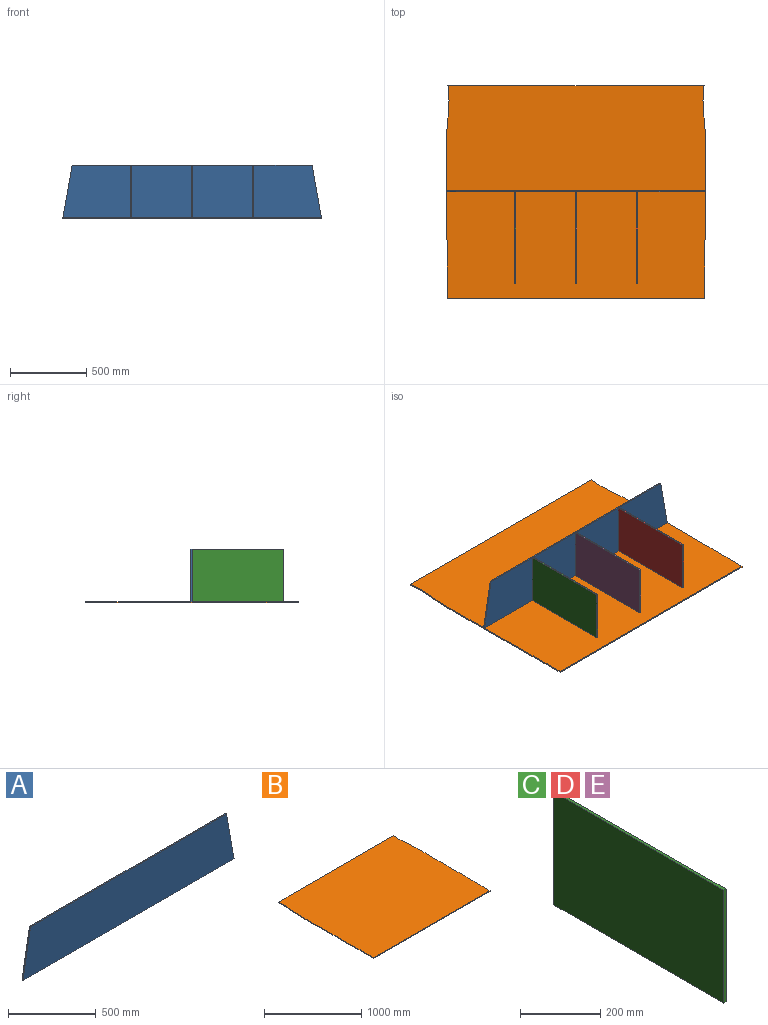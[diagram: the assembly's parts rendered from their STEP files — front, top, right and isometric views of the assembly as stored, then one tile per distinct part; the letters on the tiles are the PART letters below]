
ASSEMBLY  parts=5 mates=4
PART A: 6 faces, bbox 1700x8x344.7 mm
  f0: plane 1578.45x8mm, normal (0,0,1), area 12627.6mm2, adj f1,f3,f4,f5
  f1: plane 344.68x60.78mm, normal (-0.98,0,0.17), area 2800mm2, adj f0,f2,f4,f5
  f2: plane 1700x8mm, normal (0,0,-1), area 13600mm2, adj f1,f3,f4,f5
  f3: plane 344.68x60.78mm, normal (0.98,0,0.17), area 2800mm2, adj f0,f2,f4,f5
  f4: plane 1700x344.68mm, normal (0,-1,0), area 565011.9mm2, adj f0,f1,f2,f3
  f5: plane 1700x344.68mm, normal (0,1,0), area 565011.9mm2, adj f0,f1,f2,f3
PART B: 26 faces, bbox 1702x1400x8 mm
  f0: plane 1692x8mm, normal (0,-1,0), area 13536mm2, adj f1,f23,f24,f25
  f1: plane 100x8mm, normal (1,-0.01,0), area 800mm2, adj f0,f2,f24,f25
  f2: plane 100x8mm, normal (1,0,0), area 800mm2, adj f1,f3,f24,f25
  f3: plane 100x8mm, normal (1,-0.01,0), area 800mm2, adj f2,f4,f24,f25
  f4: plane 200x8mm, normal (1,0,0), area 1600mm2, adj f3,f5,f24,f25
  f5: plane 200x8mm, normal (1,0,0), area 1600mm2, adj f4,f6,f24,f25
  f6: plane 200x8mm, normal (1,-0.01,0), area 1600.1mm2, adj f5,f7,f24,f25
  f7: plane 100x8mm, normal (1,0,0), area 800mm2, adj f6,f8,f24,f25
  f8: plane 100x8mm, normal (1,0.01,0), area 800mm2, adj f7,f9,f24,f25
  f9: plane 100x9mm, normal (1,0.09,0), area 803.2mm2, adj f8,f10,f24,f25
  f10: plane 100x8mm, normal (1,0.06,0), area 801.4mm2, adj f9,f11,f24,f25
  f11: plane 100x8mm, normal (1,-0.07,0), area 802mm2, adj f10,f12,f24,f25
  f12: plane 1684x8mm, normal (0,1,0), area 13472mm2, adj f11,f13,f24,f25
  f13: plane 100x8mm, normal (-1,-0.07,0), area 802mm2, adj f12,f14,f24,f25
  f14: plane 100x8mm, normal (-1,0.06,0), area 801.4mm2, adj f13,f15,f24,f25
  f15: plane 100x9mm, normal (-1,0.09,0), area 803.2mm2, adj f14,f16,f24,f25
  f16: plane 100x8mm, normal (-1,0.01,0), area 800mm2, adj f15,f17,f24,f25
  f17: plane 100x8mm, normal (-1,0,0), area 800mm2, adj f16,f18,f24,f25
  f18: plane 200x8mm, normal (-1,-0.01,0), area 1600.1mm2, adj f17,f19,f24,f25
  f19: plane 200x8mm, normal (-1,0,0), area 1600mm2, adj f18,f20,f24,f25
  f20: plane 200x8mm, normal (-1,0,0), area 1600mm2, adj f19,f21,f24,f25
  f21: plane 100x8mm, normal (-1,-0.01,0), area 800mm2, adj f20,f22,f24,f25
  f22: plane 100x8mm, normal (-1,0,0), area 800mm2, adj f21,f23,f24,f25
  f23: plane 100x8mm, normal (-1,-0.01,0), area 800mm2, adj f0,f22,f24,f25
  f24: plane 1702x1400mm, normal (0,0,-1), area 2371900mm2, adj f0,f1,f2,f3,f4,f5,f6,f7
  f25: plane 1702x1400mm, normal (0,0,1), area 2371900mm2, adj f0,f1,f2,f3,f4,f5,f6,f7
PART C: 6 faces, bbox 8x600x344.7 mm
  f0: plane 600x8mm, normal (0,0,1), area 4800mm2, adj f1,f3,f4,f5
  f1: plane 344.68x8mm, normal (0,-1,0), area 2757.5mm2, adj f0,f2,f4,f5
  f2: plane 600x8mm, normal (0,0,-1), area 4800mm2, adj f1,f3,f4,f5
  f3: plane 344.68x8mm, normal (0,1,0), area 2757.5mm2, adj f0,f2,f4,f5
  f4: plane 600x344.68mm, normal (1,0,0), area 206809.6mm2, adj f0,f1,f2,f3
  f5: plane 600x344.68mm, normal (-1,0,0), area 206809.6mm2, adj f0,f1,f2,f3
PART D: same geometry as C
PART E: same geometry as C
PLACE A t=(3.79,605.93,181)mm
PLACE B t=(2.79,-2.07,181)mm
PLACE C t=(-396.21,-2.07,353.34)mm
PLACE D t=(403.79,-2.07,353.34)mm
PLACE E t=(3.79,-2.07,353.34)mm
MATE fastened A.f2 <-> B.f25  axis (0,0,1) through (-846.21,597.93,181)mm
MATE fastened C.f3 <-> A.f4  axis (0,1,0) through (3.79,597.93,181)mm
MATE fastened E.f3 <-> A.f4  axis (0,1,0) through (3.79,597.93,181)mm
MATE fastened D.f3 <-> A.f4  axis (0,1,0) through (403.79,597.93,181)mm
